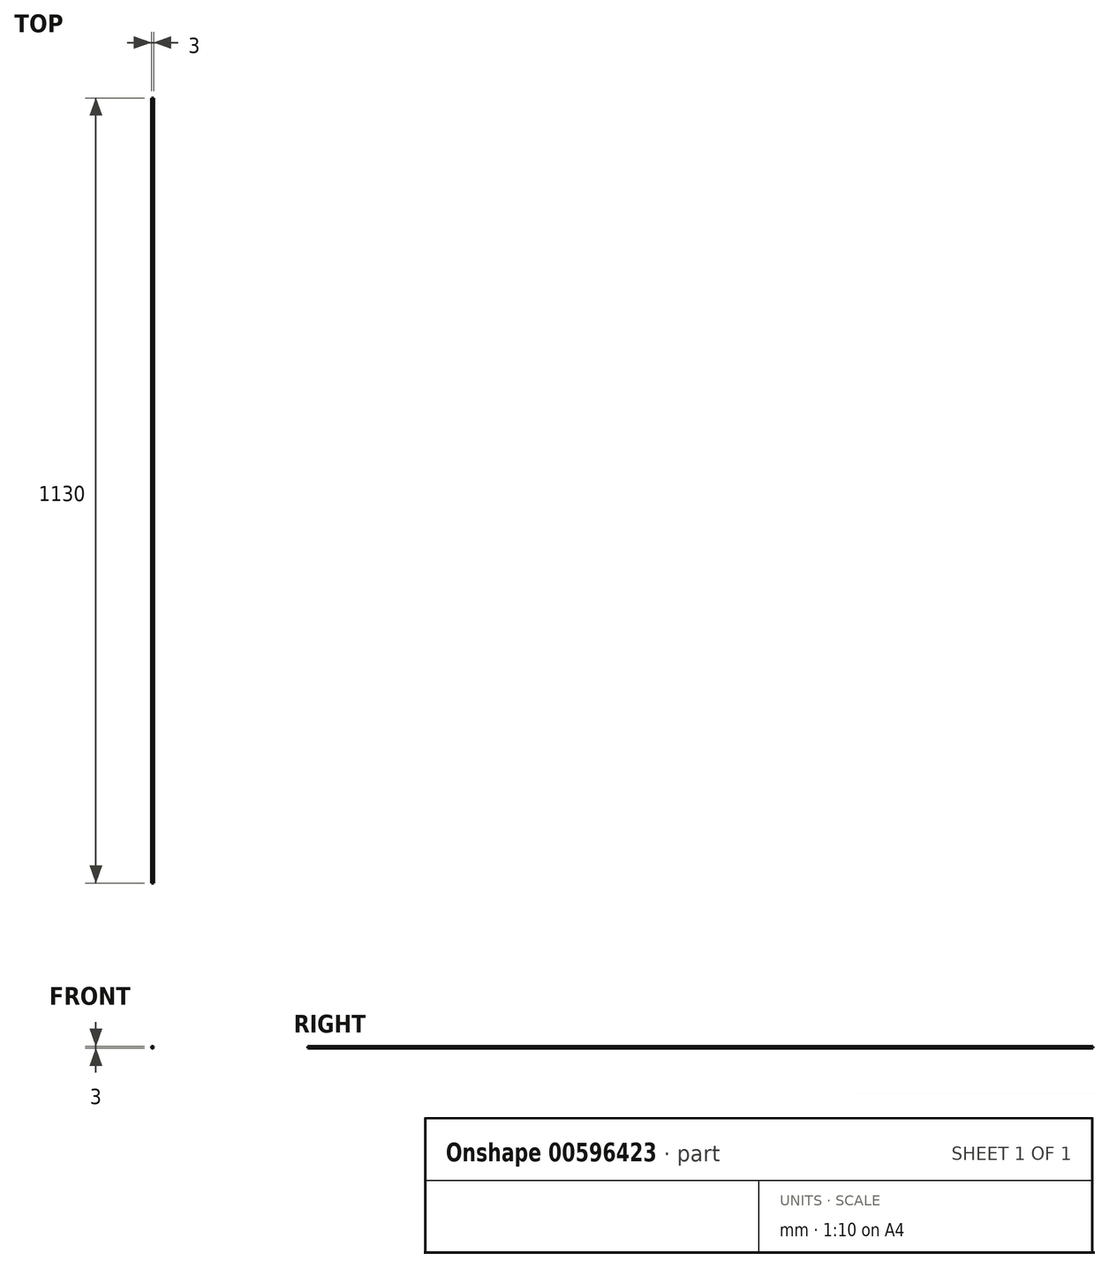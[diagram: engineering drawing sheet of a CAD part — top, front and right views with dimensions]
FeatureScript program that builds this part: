
annotation { "Feature Type Name" : "Feature", "Feature Type Description" : "" }
export const myFeature = defineFeature(function(context is Context, id is Id, definition is map)
    precondition{}
    {
        {
            var Q0;
            Q0=qCreatedBy(makeId("Front.planeOp"),FACE);
            var sketch = newSketch(context, id + "F0", { "sketchPlane" : qUnion([Q0])});
            skCircle(sketch, "E0", {"center": v(0, 0) * mm, "radius": 1.5 * mm});
            skSolve(sketch);
        }
        {
            var Q0;
            Q0=makeQuery(id+"F0.imprint","IMPRINT",FACE,{"disambiguationData":[TD([[makeQuery(id+"F0.imprint","IMPRINT",EDGE,{"derivedFrom":sQuery(id+"F0.wireOp",EDGE,"E0")}),1.0]])]});
            extrude(context, id + "F1", {"entities" : qUnion([Q0]), "depth" : 1130 * mm, "offsetDistance" : 25 * mm});
        }
    });
